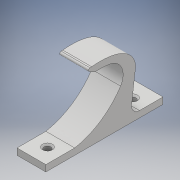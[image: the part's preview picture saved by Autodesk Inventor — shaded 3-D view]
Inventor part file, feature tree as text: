
AUTODESK INVENTOR PART (.ipt)
format: ipt  version: 2018 (Build 220112000, 112)  size: 295,936 bytes
history: native  units: mm
features: sketch x10, extrude x10, fillet x7, other x1, chamfer x1, projected_geometry x1
ambient origin geometry x8: Origin, YZ Plane, XZ Plane, XY Plane, X Axis, Y Axis, Z Axis, Center Point
bodies: Body1 (feature_tree)
feature tree (30):
  other  "Sólido1"
  sketch  "Boceto1"  dims[d0=70.0mm d1=30.0mm]
  extrude  "Extrusión1"  Depth=30.0mm
  extrude  "Extrusión2"  Depth=3.0mm
  fillet  "Empalme5"  Radius=6.5mm
  fillet  "Empalme6"  Radius=3.0mm
  extrude  "Extrusión3"  Depth=2.0mm
  extrude  "Extrusión4"  Depth=24.707127mm
  extrude  "Extrusión5"  Depth=6.0mm
  sketch  "Boceto6"  dims[d19=6.0mm d20=2.0mm]
  extrude  "Extrusión6"  Depth=2.0mm
  extrude  "Extrusión7"  Depth=10.0mm
  extrude  "Extrusión8"  Depth=6.0mm TaperAngle=0.0deg
  extrude  "Extrusión9"  Depth=34.801227mm
  extrude  "Extrusión10"  Depth=5.0mm
  chamfer  "Chaflán1"  Distance=11.065865mm
  fillet  "Empalme8"  Radius=32.656076mm
  fillet  "Empalme1"  Radius=12.532201mm
  fillet  "Empalme2"  Radius=43.52011mm
  fillet  "Empalme3"  Radius=10.605473mm
  fillet  "Empalme4"  Radius=3.516283mm
  sketch  "Boceto2"  dims[d2=4.0mm d3=6.5mm d4=6.5mm d5=3.0mm d6=0.0mm]
  sketch  "Boceto3"  dims[d7=2.0mm d8=2.0mm]
  projected_geometry  "Contorno proyectado1"
  sketch  "Boceto4"  dims[d9=12.0mm d10=24.707127mm]
  sketch  "Boceto5"  dims[d11=0.0mm d12=0.0mm d18=6.0mm]
  sketch  "Boceto7"  dims[d24=0.3mm d25=10.0mm]
  sketch  "Boceto8"  dims[d26=1.0mm d27=6.0mm d28=0.0mm]
  sketch  "Boceto9"  dims[d29=6.0mm d30=0.0mm d32=34.801227mm]
  sketch  "Boceto10"  dims[d33=12.081226mm d34=9.119372mm d35=11.065865mm d36=32.656076mm d37=12.532201mm d38=43.52011mm d39=10.605473mm d40=3.516283mm d41=6.744794mm d42=34.800749mm d43=20.382641mm d44=1.65838mm d45=16.555964mm d46=13.371162mm d47=7.0mm d48=0.0mm d51=10.0mm d52=7.0mm d53=0.0mm d54=10.0mm d55=7.0mm d56=0.0mm d57=7.0mm d58=0.0mm d59=1.0mm d60=0.0mm d61=1.0mm d62=0.0mm d63=1.0mm d64=2.0mm d65=45.0deg d66=4.2mm d67=15.201603mm d68=15.0mm d69=5.0mm]
